# Revit family: Hager-Gamma-IP30-sistema-CH-it
name_source: partatom
category: Electrical Equipment
units: mm (PartAtom-declared; Revit-internal decimal feet)

## family parameters
Cut with Voids When Loaded = No
Host = Face
Panel Configuration = Two Columns, Circuits Across
Part Type = Panelboard
Room Calculation Point = No
Round Connector Dimension = Use Diameter
Shared = No

## types (4) — shared parameters
EF000003 - Tipo di montaggio = EV000384 - A parete
EF000007 - colore = EV000202 - bianco
EF000008 - Larghezza = 250 mm  [stored 0.82021 ft]
EF000049 - profondità = 103 mm  [stored 0.337927 ft]
EF000116 - numero RAL = 9010
EF000118 - con piastra di montaggio = No
EF000339 - tipo di copertura = EV001012 - coperchio
EF001062 - esecuzione EMC = No
EF001088 - possibilità di applicazione = Yes
EF001134 - barra DIN = Yes
EF001596 - Attacco Lampada = EV000139 - plastica
EF002950 - Numero moduli DIN = 13
EF004462 - tipo di chiusura = EV000154 - altri
EF005474 - grado di protezione (IP) = EV006410 - IP30
EF006244 - coperchio/porta trasparente = No
EF006306 - con serratura = No
EF009212 - esecuzione coperchio = EV009916 - con taglio
HG000001 - Numero di colonne = 1
HG000002 - Con porta = No
HG000003 - Gamma = Gamma
HG000005 - Spessore = 3 mm  [stored 0.00984252 ft]
HG000006 - Ad incasso = No
HG000009 - Porta doppia a battente = No
HG000010 - Porte asimmetriche = No
HG000011 - File vuote nella parte basse = No
HG000017 - Distanza tra i poli = 18 mm  [stored 0.0590551 ft]
Manufacturer = Hager
Type Comments = Gamma
zero-valued in all types: Default Elevation, EF000218 - profondità di incasso, EF000332 - Altezza della parte incassata, EF000846 - larghezza di montaggio, EF001131 - profondità interna, HG000007 - Numero di colonne vuote, HG000008 - Numero di file vuote

## per-type parameters (varying)
| type | EF000040 - Altezza | EF000266 - numero di file | EF015776 - Morsettiera di terra | EF015777 - Morsettiera neutra | EF015941 - Segnale di passaggio porta | HG000004 - Codice produttore | Model |
| A parete IP30 L250 A250 P103 13 Unità di divisione - GD113G | 250 mm  [stored 0.82021 ft] | 1 | Yes | Yes | Yes | GD113G | GD113G |
| A parete IP30 L250 A375 P103 13 Unità di divisione - GD213G | 375 mm | 2 | No | No | No | GD213G | GD213G |
| A parete IP30 L250 A500 P103 13 Unità di divisione - GD313G | 500 mm  [stored 1.64042 ft] | 3 | No | No | No | GD313G | GD313G |
| A parete IP30 L250 A625 P103 13 Unità di divisione - GD413G | 625 mm  [stored 2.05052 ft] | 4 | No | No | No | GD413G | GD413G |

note: [stored X ft] marks values corroborated as IEEE doubles in the binary element streams (Revit-internal decimal feet)

## geometry (parser evidence)
native form markers: Sweep x17
no freeform markers — native parametric forms only
